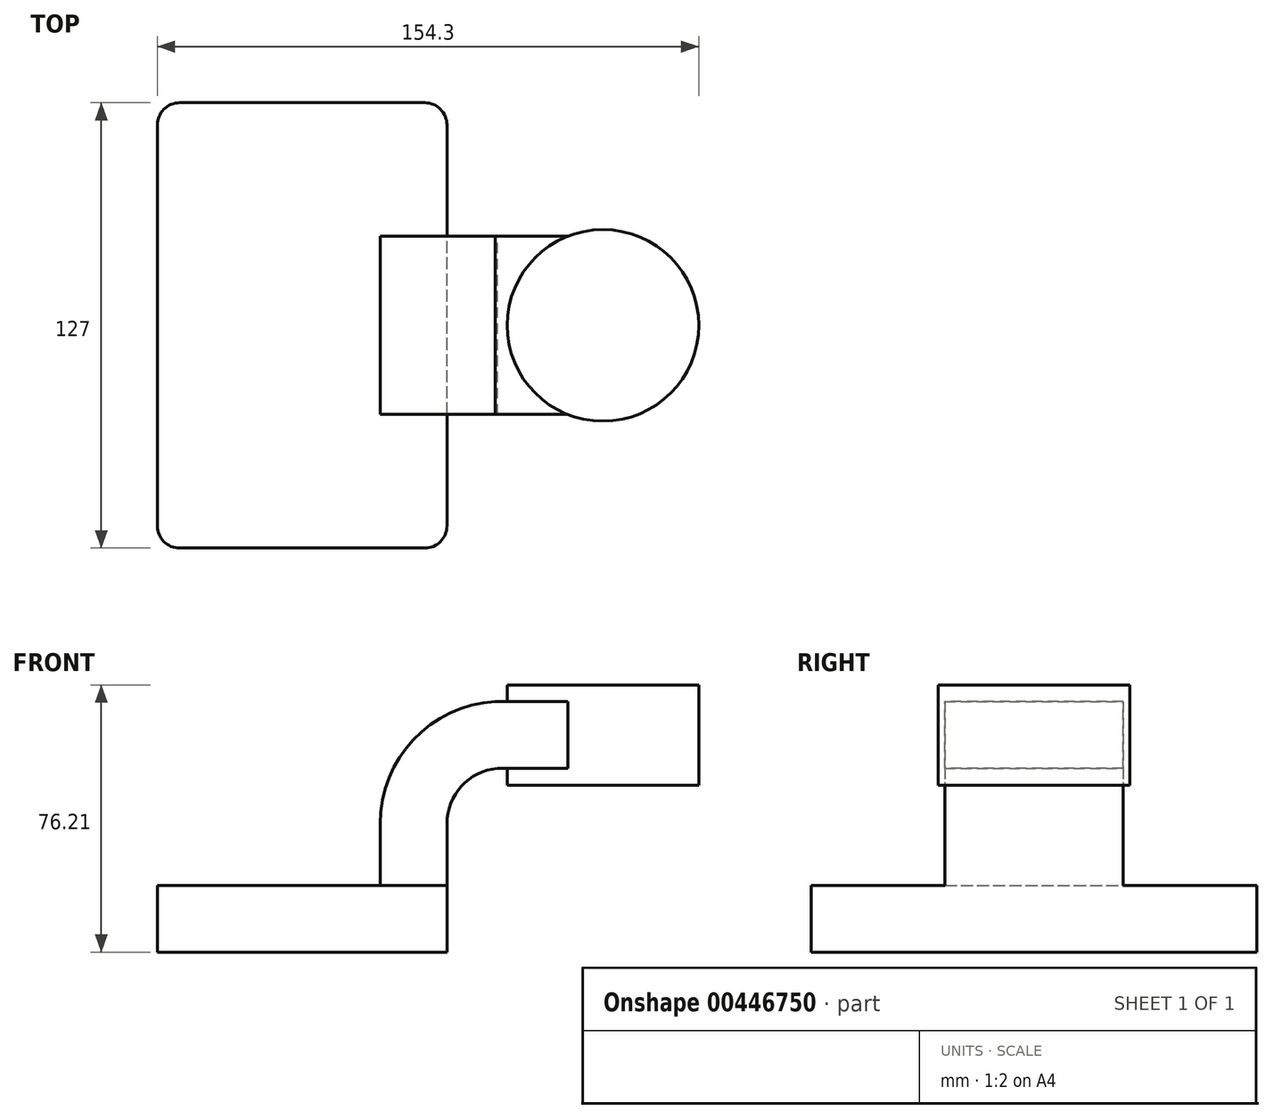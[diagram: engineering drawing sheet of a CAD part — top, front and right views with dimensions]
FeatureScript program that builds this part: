
annotation { "Feature Type Name" : "Feature", "Feature Type Description" : "" }
export const myFeature = defineFeature(function(context is Context, id is Id, definition is map)
    precondition{}
    {
        {
            var Q0;
            Q0=qCreatedBy(makeId("Front.planeOp"),FACE);
            var sketch = newSketch(context, id + "F0", { "sketchPlane" : qUnion([Q0])});
            skLineSegment(sketch, "E0.bottom", {"start": v(41.27, -9.52) * mm, "end": v(-41.27, -9.53) * mm});
            skLineSegment(sketch, "E0.top", {"start": v(41.27, 9.53) * mm, "end": v(-41.28, 9.52) * mm});
            skLineSegment(sketch, "E0.left", {"start": v(41.27, -9.52) * mm, "end": v(41.27, 9.53) * mm});
            skLineSegment(sketch, "E0.right", {"start": v(-41.28, -9.53) * mm, "end": v(-41.28, 9.52) * mm});
            skPoint(sketch, "E0.middle", {"position": v(0, 0) * mm});
            skLineSegment(sketch, "E1.bottom", {"start": v(113.03, 66.68) * mm, "end": v(62.23, 66.68) * mm});
            skLineSegment(sketch, "E1.top", {"start": v(113.03, 38.1) * mm, "end": v(62.23, 38.1) * mm});
            skLineSegment(sketch, "E1.left", {"start": v(113.03, 66.68) * mm, "end": v(113.03, 38.1) * mm});
            skLineSegment(sketch, "E1.right", {"start": v(62.23, 66.68) * mm, "end": v(62.23, 38.1) * mm});
            skPoint(sketch, "E1.middle", {"position": v(87.63, 52.39) * mm});
            skLineSegment(sketch, "E2", {"start": v(41.27, 9.53) * mm, "end": v(41.27, 27.07) * mm});
            skArc(sketch, "E3", {"start": v(41.28, 27.07) * mm, "mid": v(45.42, 37.77) * mm, "end": v(55.7, 42.88) * mm});
            skLineSegment(sketch, "E4", {"start": v(55.7, 42.88) * mm, "end": v(85.73, 42.88) * mm});
            skLineSegment(sketch, "E5.0", {"start": v(55, 61.93) * mm, "end": v(85.73, 61.93) * mm});
            skArc(sketch, "E5.1", {"start": v(22.23, 27.07) * mm, "mid": v(31.7, 51) * mm, "end": v(55, 61.93) * mm});
            skLineSegment(sketch, "E5.2", {"start": v(22.23, 9.53) * mm, "end": v(22.23, 27.07) * mm});
            skPoint(sketch, "E6", {"position": v(87.63, 38.1) * mm});
            skLineSegment(sketch, "E7", {"start": v(85.73, 66.68) * mm, "end": v(85.73, 38.1) * mm});
            skFitSpline(sketch, "E8", {"points": [v(-41.28, 9.52) * mm, v(55, 61.93) * mm], "startDerivative": vector(1.49, 135.24) * mm, "endDerivative": vector(146.85, 3.76) * mm});
            skSolve(sketch);
        }
        {
            var Q0;
            Q0=makeQuery(id+"F0.imprint","IMPRINT",FACE,{"disambiguationData":[TD([[makeQuery(id+"F0.imprint","IMPRINT",EDGE,{"derivedFrom":sQuery(id+"F0.wireOp",EDGE,"E0.bottom")}),-1.0]])]});
            extrude(context, id + "F1", {"entities" : qUnion([Q0]), "endBound" : BoundingType.SYMMETRIC, "depth" : 127 * mm});
        }
        {
            var Q0;
            {var subQ1=sQuery(id+"F0.wireOp",EDGE,"E2");Q0=makeQuery(id+"F0.imprint","IMPRINT",FACE,{"disambiguationData":[TD([[makeQuery(id+"F0.imprint","IMPRINT",EDGE,{"derivedFrom":subQ1}),1.0]])]});}
            var Q1;
            {var subQ0=sQuery(id+"F0.wireOp",EDGE,"E5.0");var subQ1=sQuery(id+"F0.wireOp",EDGE,"E1.right");var subQ2=makeQuery(id+"F0.imprint","INTERSECT",VERTEX,{"derivedFrom":[subQ1,subQ0]});Q1=makeQuery(id+"F0.imprint","IMPRINT",FACE,{"disambiguationData":[TD([[makeQuery(id+"F0.imprint","IMPRINT",EDGE,{"disambiguationData":[TD([[subQ2,-1.0]])],"derivedFrom":subQ1}),1.0]])]});}
            extrude(context, id + "F2", {"entities" : qUnion([Q0, Q1]), "operationType" : NewBodyOperationType.ADD, "endBound" : BoundingType.SYMMETRIC, "depth" : 50.8 * mm});
        }
        {
            var Q0;
            Q0=makeQuery(id+"F0.imprint","IMPRINT",FACE,{"disambiguationData":[TD([[makeQuery(id+"F0.imprint","IMPRINT",EDGE,{"derivedFrom":sQuery(id+"F0.wireOp",EDGE,"E5.1")}),1.0]])]});
            extrude(context, id + "F3", {"entities" : qUnion([Q0]), "operationType" : NewBodyOperationType.ADD, "depth" : 15.88 * mm});
        }
        {
            var Q0;
            {var subQ4=sQuery(id+"F0.wireOp",EDGE,"E1.left");Q0=makeQuery(id+"F0.imprint","IMPRINT",FACE,{"disambiguationData":[TD([[makeQuery(id+"F0.imprint","IMPRINT",EDGE,{"derivedFrom":subQ4}),-1.0]])]});}
            var Q1;
            Q1=sQuery(id+"F0.wireOp",EDGE,"E7");
            revolve(context, id + "F4", {"operationType" : NewBodyOperationType.ADD, "entities" : qUnion([Q0]), "axis" : qUnion([Q1]), "revolveType" : RevolveType.FULL});
        }
        {
            var Q0;
            Q0=makeQuery(id+"F1.opExtrude","CAP_EDGE",EDGE,{"disambiguationData":[OSD([sQuery(id+"F0.wireOp",EDGE,"E0.right")])],"isStart":false});
            var Q1;
            Q1=makeQuery(id+"F1.opExtrude","CAP_EDGE",EDGE,{"disambiguationData":[OSD([sQuery(id+"F0.wireOp",EDGE,"E0.left")])],"isStart":false});
            var Q2;
            Q2=makeQuery(id+"F1.opExtrude","CAP_EDGE",EDGE,{"disambiguationData":[OSD([sQuery(id+"F0.wireOp",EDGE,"E0.left")])],"isStart":true});
            var Q3;
            Q3=makeQuery(id+"F1.opExtrude","CAP_EDGE",EDGE,{"disambiguationData":[OSD([sQuery(id+"F0.wireOp",EDGE,"E0.right")])],"isStart":true});
            fillet(context, id + "F5", {"entities" : qUnion([Q0, Q1, Q2, Q3]), "radius" : 6.35 * mm, "tangentPropagation" : true, "allowEdgeOverflow" : false});
        }
    });
